# Revit family: Casement_36_G_Top_Hung_Standard
name_source: partatom
category: Windows
revit_build: Autodesk Revit 2014 (Build: 20130308_1515(x64)
units: mm (PartAtom-declared; Revit-internal decimal feet)

## types (12) — shared parameters
Aluminium Thickness = 1 mm  [stored 0.00328084 ft]
Bead SG Gap = 13 mm  [stored 0.0426509 ft]
Bottom Hung = No
Casement Dimension = 36 mm  [stored 0.11811 ft]
Custom Sash Height Bottom = 569 mm  [stored 1.8668 ft]
Custom Sash Height Top = 569 mm  [stored 1.8668 ft]
Custom Window Height = 1190 mm  [stored 3.9042 ft]
DG Extrusion Start = 8 mm  [stored 0.0262467 ft]
DG Gasket Finish = Double Glazing Gasket Material
DG Thickness Calc = 4 mm  [stored 0.0131234 ft]
Default Sill Height = 800 mm  [stored 2.62467 ft]
Depth Bead = 22 mm  [stored 0.0721785 ft]
Description = Window 36mm, Type G top hung
Frame Center Offset = 18 mm  [stored 0.0590551 ft]
Height = 1200 mm  [stored 3.93701 ft]
Height Panel 1 = 555 mm  [stored 1.82087 ft]
Height Panel 2 = 555 mm  [stored 1.82087 ft]
Height Panel 4 = 1140 mm  [stored 3.74016 ft]
Height Sash 1 = 539 mm
Height Sash 2 = 539 mm
Height Sash Bottom Opening = 569 mm  [stored 1.8668 ft]
Height Sash Top Opening = 569 mm  [stored 1.8668 ft]
Length Mullion = 1200 mm  [stored 3.93701 ft]
Limit Fixed Pane Height Max = 1800 mm
Limit Fixed Pane Height Min = 200 mm  [stored 0.656168 ft]
Limit Fixed Pane Width Max = 1500 mm
Limit Fixed Pane Width Min = 200 mm  [stored 0.656168 ft]
Limit Sash Bottom Height Max Based On Top Sash = 1229 mm
Limit Sash Height Bottom Max = 900 mm  [stored 2.95276 ft]
Limit Sash Height Bottom Min = 300 mm  [stored 0.984252 ft]
Limit Sash Height Top Max = 900 mm  [stored 2.95276 ft]
Limit Sash Height Top Min = 300 mm  [stored 0.984252 ft]
Limit Sash Width Max = 1200 mm  [stored 3.93701 ft]
Limit Sash Width Min = 300 mm  [stored 0.984252 ft]
Limit Window Height Max = 1860 mm
Manufacturer = Crealco
Max System DG One Piece Thickness = 6 mm  [stored 0.019685 ft]
Max System DG Unit Thickness = 25 mm  [stored 0.082021 ft]
Model = Casement 36
Offset Bead SG Center Reversed = 18 mm  [stored 0.0590551 ft]
Offset Sash 1 Top = 23 mm  [stored 0.0754593 ft]
Offset Sash 2 Top = 608 mm  [stored 1.99475 ft]
Offset Sash Left = 23 mm  [stored 0.0754593 ft]
Offset Transom 1 Top = 585 mm  [stored 1.91929 ft]
Offset Window Exterior = 18 mm  [stored 0.0590551 ft]
Rough Width = 16 mm  [stored 0.0524934 ft]
SG Gasket Thickness = 6 mm  [stored 0.019685 ft]
Sash Center Offset = 15 mm  [stored 0.0492126 ft]
Sash Overlap = 7 mm  [stored 0.0229659 ft]
Sash Spacing Inner = 8 mm  [stored 0.0262467 ft]
Top Hung = Yes
URL = http://www.crealco.co.za
Wall Closure = By host
Width Bead = 15 mm  [stored 0.0492126 ft]
Width Profile = 30 mm  [stored 0.0984252 ft]
zero-valued in all types: Window Exterior Offset

## per-type parameters (varying)
- 36-1212DT-1000Pa: Area Pane Left Bottom=0.25 m²; Area Pane Left Top=0.25 m²; Area Pane Right=0.6 m²; Clearvue Insulated LowE SHGC Value=0.639; Clearvue Insulated LowE U Value=4.92; Clearvue Insulated SHGC Value=0.7; Clearvue Insulated U Value=5.59; Clearvue SHGC Value=0.796; Clearvue U Value=8.34; Custom Sash Width=569 mm  [stored 1.8668 ft]; Custom Windload=1000 mm  [stored 3.28084 ft]; Custom Window Width=1190 mm  [stored 3.9042 ft]; Depth Mullion=37 mm  [stored 0.121391 ft]; Energy Advantage SHGC Value=0.714; Energy Advantage U Value=6.46; Intruderprufe Insulated LowE SHGC Value=0.591; Intruderprufe Insulated LowE U Value=4.81; Intruderprufe Insulated SHGC Value=0.643; Intruderprufe Insulated U Value=5.45; Intruderprufe LowE SHGC Value=0.669; Intruderprufe LowE U Value=6.31; Intruderprufe SHGC Value=0.759; Intruderprufe U Value=8.16; Length Transom=555 mm  [stored 1.82087 ft]; Limit Window Width Max=2145 mm; Limit Window Width Min=845 mm  [stored 2.77231 ft]; Max Pane Area=0.6 m²; Mullion Depth Windload Based=37 mm  [stored 0.121391 ft]; Offset Mullion Left=585 mm  [stored 1.91929 ft]; Offset Panel 4 Left=615 mm  [stored 2.01772 ft]; Width=1190 mm  [stored 3.9042 ft]; Width Panel 1=555 mm  [stored 1.82087 ft]; Width Panel 2=555 mm  [stored 1.82087 ft]; Width Panel 4=545 mm; Width Sash 1=539 mm; Width Sash 2=539 mm; Width Sash Opening=569 mm  [stored 1.8668 ft]; Windload Design=1000 mm  [stored 3.28084 ft]
- 36-1512DT-1000Pa: Area Pane Left Bottom=0.25 m²; Area Pane Left Top=0.25 m²; Area Pane Right=0.94 m²; Clearvue Insulated LowE SHGC Value=0.73; Clearvue Insulated LowE U Value=4.85; Clearvue Insulated SHGC Value=0.8; Clearvue Insulated U Value=5.63; Clearvue SHGC Value=0.909; Clearvue U Value=8.83; Custom Sash Width=569 mm  [stored 1.8668 ft]; Custom Windload=1000 mm  [stored 3.28084 ft]; Custom Window Width=1490 mm; Depth Mullion=37 mm  [stored 0.121391 ft]; Energy Advantage SHGC Value=0.814; Energy Advantage U Value=6.64; Intruderprufe Insulated LowE SHGC Value=0.671; Intruderprufe Insulated LowE U Value=4.74; Intruderprufe Insulated SHGC Value=0.734; Intruderprufe Insulated U Value=5.49; Intruderprufe LowE SHGC Value=0.763; Intruderprufe LowE U Value=6.48; Intruderprufe SHGC Value=0.865; Intruderprufe U Value=8.64; Length Transom=555 mm  [stored 1.82087 ft]; Limit Window Width Max=2145 mm; Limit Window Width Min=845 mm  [stored 2.77231 ft]; Max Pane Area=0.94 m²; Mullion Depth Windload Based=37 mm  [stored 0.121391 ft]; Offset Mullion Left=585 mm  [stored 1.91929 ft]; Offset Panel 4 Left=615 mm  [stored 2.01772 ft]; Width=1490 mm; Width Panel 1=555 mm  [stored 1.82087 ft]; Width Panel 2=555 mm  [stored 1.82087 ft]; Width Panel 4=845 mm  [stored 2.77231 ft]; Width Sash 1=539 mm; Width Sash 2=539 mm; Width Sash Opening=569 mm  [stored 1.8668 ft]; Windload Design=1000 mm  [stored 3.28084 ft]
- 36-1812DT-1000Pa: Area Pane Left Bottom=0.41 m²; Area Pane Left Top=0.41 m²; Area Pane Right=0.91 m²; Clearvue Insulated LowE SHGC Value=0.687; Clearvue Insulated LowE U Value=4.47; Clearvue Insulated SHGC Value=0.753; Clearvue Insulated U Value=5.2; Clearvue SHGC Value=0.855; Clearvue U Value=8.22; Custom Sash Width=900 mm  [stored 2.95276 ft]; Custom Windload=1000 mm  [stored 3.28084 ft]; Custom Window Width=1790 mm; Depth Mullion=37 mm  [stored 0.121391 ft]; Energy Advantage SHGC Value=0.766; Energy Advantage U Value=6.15; Intruderprufe Insulated LowE SHGC Value=0.631; Intruderprufe Insulated LowE U Value=4.37; Intruderprufe Insulated SHGC Value=0.691; Intruderprufe Insulated U Value=5.08; Intruderprufe LowE SHGC Value=0.717; Intruderprufe LowE U Value=6.01; Intruderprufe SHGC Value=0.814; Intruderprufe U Value=8.04; Length Transom=886 mm  [stored 2.90682 ft]; Limit Window Width Max=2476 mm; Limit Window Width Min=1176 mm  [stored 3.85827 ft]; Max Pane Area=0.91 m²; Mullion Depth Windload Based=37 mm  [stored 0.121391 ft]; Offset Mullion Left=916 mm  [stored 3.00525 ft]; Offset Panel 4 Left=946 mm; Width=1790 mm; Width Panel 1=886 mm  [stored 2.90682 ft]; Width Panel 2=886 mm  [stored 2.90682 ft]; Width Panel 4=814 mm; Width Sash 1=870 mm  [stored 2.85433 ft]; Width Sash 2=870 mm  [stored 2.85433 ft]; Width Sash Opening=900 mm  [stored 2.95276 ft]; Windload Design=1000 mm  [stored 3.28084 ft]
- 36-2412DT-1000Pa: Area Pane Left Bottom=0.41 m²; Area Pane Left Top=0.41 m²; Area Pane Right=1.59 m²; Clearvue Insulated LowE SHGC Value=0.543; Clearvue Insulated LowE U Value=3.08; Clearvue Insulated SHGC Value=0.597; Clearvue Insulated U Value=3.67; Clearvue SHGC Value=0; Clearvue U Value=7.9; Custom Sash Width=900 mm  [stored 2.95276 ft]; Custom Windload=1000 mm  [stored 3.28084 ft]; Custom Window Width=2390 mm; Depth Mullion=37 mm  [stored 0.121391 ft]; Energy Advantage SHGC Value=0; Energy Advantage U Value=7.9; Intruderprufe Insulated LowE SHGC Value=0.499; Intruderprufe Insulated LowE U Value=3.01; Intruderprufe Insulated SHGC Value=0.548; Intruderprufe Insulated U Value=3.58; Intruderprufe LowE SHGC Value=0.567; Intruderprufe LowE U Value=4.33; Intruderprufe SHGC Value=0.644; Intruderprufe U Value=5.95; Length Transom=886 mm  [stored 2.90682 ft]; Limit Window Width Max=2476 mm; Limit Window Width Min=1176 mm  [stored 3.85827 ft]; Max Pane Area=1.59 m²; Mullion Depth Windload Based=37 mm  [stored 0.121391 ft]; Offset Mullion Left=916 mm  [stored 3.00525 ft]; Offset Panel 4 Left=946 mm; Width=2390 mm; Width Panel 1=886 mm  [stored 2.90682 ft]; Width Panel 2=886 mm  [stored 2.90682 ft]; Width Panel 4=1414 mm; Width Sash 1=870 mm  [stored 2.85433 ft]; Width Sash 2=870 mm  [stored 2.85433 ft]; Width Sash Opening=900 mm  [stored 2.95276 ft]; Windload Design=1000 mm  [stored 3.28084 ft]
- 36-1212DT-1500Pa: Area Pane Left Bottom=0.25 m²; Area Pane Left Top=0.25 m²; Area Pane Right=0.6 m²; Clearvue Insulated LowE SHGC Value=0.639; Clearvue Insulated LowE U Value=4.92; Clearvue Insulated SHGC Value=0.7; Clearvue Insulated U Value=5.59; Clearvue SHGC Value=0.796; Clearvue U Value=8.34; Custom Sash Width=569 mm  [stored 1.8668 ft]; Custom Windload=1500 mm; Custom Window Width=1190 mm  [stored 3.9042 ft]; Depth Mullion=37 mm  [stored 0.121391 ft]; Energy Advantage SHGC Value=0.714; Energy Advantage U Value=6.46; Intruderprufe Insulated LowE SHGC Value=0.591; Intruderprufe Insulated LowE U Value=4.81; Intruderprufe Insulated SHGC Value=0.643; Intruderprufe Insulated U Value=5.45; Intruderprufe LowE SHGC Value=0.669; Intruderprufe LowE U Value=6.31; Intruderprufe SHGC Value=0.759; Intruderprufe U Value=8.16; Length Transom=555 mm  [stored 1.82087 ft]; Limit Window Width Max=2145 mm; Limit Window Width Min=845 mm  [stored 2.77231 ft]; Max Pane Area=0.6 m²; Mullion Depth Windload Based=37 mm  [stored 0.121391 ft]; Offset Mullion Left=585 mm  [stored 1.91929 ft]; Offset Panel 4 Left=615 mm  [stored 2.01772 ft]; Width=1190 mm  [stored 3.9042 ft]; Width Panel 1=555 mm  [stored 1.82087 ft]; Width Panel 2=555 mm  [stored 1.82087 ft]; Width Panel 4=545 mm; Width Sash 1=539 mm; Width Sash 2=539 mm; Width Sash Opening=569 mm  [stored 1.8668 ft]; Windload Design=1500 mm
- 36-1212DT-2000Pa: Area Pane Left Bottom=0.25 m²; Area Pane Left Top=0.25 m²; Area Pane Right=0.6 m²; Clearvue Insulated LowE SHGC Value=0.639; Clearvue Insulated LowE U Value=4.96; Clearvue Insulated SHGC Value=0.701; Clearvue Insulated U Value=5.62; Clearvue SHGC Value=0.798; Clearvue U Value=8.4; Custom Sash Width=569 mm  [stored 1.8668 ft]; Custom Windload=2000 mm; Custom Window Width=1190 mm  [stored 3.9042 ft]; Depth Mullion=54 mm  [stored 0.177165 ft]; Energy Advantage SHGC Value=0.716; Energy Advantage U Value=6.53; Intruderprufe Insulated LowE SHGC Value=0.59; Intruderprufe Insulated LowE U Value=4.86; Intruderprufe Insulated SHGC Value=0.644; Intruderprufe Insulated U Value=5.5; Intruderprufe LowE SHGC Value=0.671; Intruderprufe LowE U Value=6.39; Intruderprufe SHGC Value=0.762; Intruderprufe U Value=8.23; Length Transom=555 mm  [stored 1.82087 ft]; Limit Window Width Max=2145 mm; Limit Window Width Min=845 mm  [stored 2.77231 ft]; Max Pane Area=0.6 m²; Mullion Depth Windload Based=54 mm  [stored 0.177165 ft]; Offset Mullion Left=585 mm  [stored 1.91929 ft]; Offset Panel 4 Left=615 mm  [stored 2.01772 ft]; Width=1190 mm  [stored 3.9042 ft]; Width Panel 1=555 mm  [stored 1.82087 ft]; Width Panel 2=555 mm  [stored 1.82087 ft]; Width Panel 4=545 mm; Width Sash 1=539 mm; Width Sash 2=539 mm; Width Sash Opening=569 mm  [stored 1.8668 ft]; Windload Design=2000 mm
- 36-1512DT-1500Pa: Area Pane Left Bottom=0.25 m²; Area Pane Left Top=0.25 m²; Area Pane Right=0.94 m²; Clearvue Insulated LowE SHGC Value=0.728; Clearvue Insulated LowE U Value=4.91; Clearvue Insulated SHGC Value=0.799; Clearvue Insulated U Value=5.68; Clearvue SHGC Value=0.908; Clearvue U Value=8.87; Custom Sash Width=569 mm  [stored 1.8668 ft]; Custom Windload=1500 mm; Custom Window Width=1490 mm; Depth Mullion=54 mm  [stored 0.177165 ft]; Energy Advantage SHGC Value=0.813; Energy Advantage U Value=6.68; Intruderprufe Insulated LowE SHGC Value=0.672; Intruderprufe Insulated LowE U Value=4.8; Intruderprufe Insulated SHGC Value=0.733; Intruderprufe Insulated U Value=5.55; Intruderprufe LowE SHGC Value=0.761; Intruderprufe LowE U Value=6.53; Intruderprufe SHGC Value=0.864; Intruderprufe U Value=8.67; Length Transom=555 mm  [stored 1.82087 ft]; Limit Window Width Max=2145 mm; Limit Window Width Min=845 mm  [stored 2.77231 ft]; Max Pane Area=0.94 m²; Mullion Depth Windload Based=54 mm  [stored 0.177165 ft]; Offset Mullion Left=585 mm  [stored 1.91929 ft]; Offset Panel 4 Left=615 mm  [stored 2.01772 ft]; Width=1490 mm; Width Panel 1=555 mm  [stored 1.82087 ft]; Width Panel 2=555 mm  [stored 1.82087 ft]; Width Panel 4=845 mm  [stored 2.77231 ft]; Width Sash 1=539 mm; Width Sash 2=539 mm; Width Sash Opening=569 mm  [stored 1.8668 ft]; Windload Design=1500 mm
- 36-1512DT-2000Pa: Area Pane Left Bottom=0.25 m²; Area Pane Left Top=0.25 m²; Area Pane Right=0.94 m²; Clearvue Insulated LowE SHGC Value=0.728; Clearvue Insulated LowE U Value=4.91; Clearvue Insulated SHGC Value=0.799; Clearvue Insulated U Value=5.68; Clearvue SHGC Value=0.908; Clearvue U Value=8.87; Custom Sash Width=569 mm  [stored 1.8668 ft]; Custom Windload=2000 mm; Custom Window Width=1490 mm; Depth Mullion=54 mm  [stored 0.177165 ft]; Energy Advantage SHGC Value=0.813; Energy Advantage U Value=6.68; Intruderprufe Insulated LowE SHGC Value=0.672; Intruderprufe Insulated LowE U Value=4.8; Intruderprufe Insulated SHGC Value=0.733; Intruderprufe Insulated U Value=5.55; Intruderprufe LowE SHGC Value=0.761; Intruderprufe LowE U Value=6.53; Intruderprufe SHGC Value=0.864; Intruderprufe U Value=8.67; Length Transom=555 mm  [stored 1.82087 ft]; Limit Window Width Max=2145 mm; Limit Window Width Min=845 mm  [stored 2.77231 ft]; Max Pane Area=0.94 m²; Mullion Depth Windload Based=54 mm  [stored 0.177165 ft]; Offset Mullion Left=585 mm  [stored 1.91929 ft]; Offset Panel 4 Left=615 mm  [stored 2.01772 ft]; Width=1490 mm; Width Panel 1=555 mm  [stored 1.82087 ft]; Width Panel 2=555 mm  [stored 1.82087 ft]; Width Panel 4=845 mm  [stored 2.77231 ft]; Width Sash 1=539 mm; Width Sash 2=539 mm; Width Sash Opening=569 mm  [stored 1.8668 ft]; Windload Design=2000 mm
- 36-1812DT-1500Pa: Area Pane Left Bottom=0.41 m²; Area Pane Left Top=0.41 m²; Area Pane Right=0.91 m²; Clearvue Insulated LowE SHGC Value=0.685; Clearvue Insulated LowE U Value=4.51; Clearvue Insulated SHGC Value=0.752; Clearvue Insulated U Value=5.25; Clearvue SHGC Value=0.854; Clearvue U Value=8.25; Custom Sash Width=900 mm  [stored 2.95276 ft]; Custom Windload=1500 mm; Custom Window Width=1790 mm; Depth Mullion=54 mm  [stored 0.177165 ft]; Energy Advantage SHGC Value=0.765; Energy Advantage U Value=6.19; Intruderprufe Insulated LowE SHGC Value=0.632; Intruderprufe Insulated LowE U Value=4.41; Intruderprufe Insulated SHGC Value=0.69; Intruderprufe Insulated U Value=5.12; Intruderprufe LowE SHGC Value=0.716; Intruderprufe LowE U Value=6.05; Intruderprufe SHGC Value=0.813; Intruderprufe U Value=8.07; Length Transom=886 mm  [stored 2.90682 ft]; Limit Window Width Max=2476 mm; Limit Window Width Min=1176 mm  [stored 3.85827 ft]; Max Pane Area=0.91 m²; Mullion Depth Windload Based=54 mm  [stored 0.177165 ft]; Offset Mullion Left=916 mm  [stored 3.00525 ft]; Offset Panel 4 Left=946 mm; Width=1790 mm; Width Panel 1=886 mm  [stored 2.90682 ft]; Width Panel 2=886 mm  [stored 2.90682 ft]; Width Panel 4=814 mm; Width Sash 1=870 mm  [stored 2.85433 ft]; Width Sash 2=870 mm  [stored 2.85433 ft]; Width Sash Opening=900 mm  [stored 2.95276 ft]; Windload Design=1500 mm
- 36-1812DT-2000Pa: Area Pane Left Bottom=0.41 m²; Area Pane Left Top=0.41 m²; Area Pane Right=0.91 m²; Clearvue Insulated LowE SHGC Value=0.685; Clearvue Insulated LowE U Value=4.51; Clearvue Insulated SHGC Value=0.752; Clearvue Insulated U Value=5.25; Clearvue SHGC Value=0.854; Clearvue U Value=8.25; Custom Sash Width=900 mm  [stored 2.95276 ft]; Custom Windload=2000 mm; Custom Window Width=1790 mm; Depth Mullion=54 mm  [stored 0.177165 ft]; Energy Advantage SHGC Value=0.765; Energy Advantage U Value=6.19; Intruderprufe Insulated LowE SHGC Value=0.632; Intruderprufe Insulated LowE U Value=4.41; Intruderprufe Insulated SHGC Value=0.69; Intruderprufe Insulated U Value=5.12; Intruderprufe LowE SHGC Value=0.716; Intruderprufe LowE U Value=6.05; Intruderprufe SHGC Value=0.813; Intruderprufe U Value=8.07; Length Transom=886 mm  [stored 2.90682 ft]; Limit Window Width Max=2476 mm; Limit Window Width Min=1176 mm  [stored 3.85827 ft]; Max Pane Area=0.91 m²; Mullion Depth Windload Based=54 mm  [stored 0.177165 ft]; Offset Mullion Left=916 mm  [stored 3.00525 ft]; Offset Panel 4 Left=946 mm; Width=1790 mm; Width Panel 1=886 mm  [stored 2.90682 ft]; Width Panel 2=886 mm  [stored 2.90682 ft]; Width Panel 4=814 mm; Width Sash 1=870 mm  [stored 2.85433 ft]; Width Sash 2=870 mm  [stored 2.85433 ft]; Width Sash Opening=900 mm  [stored 2.95276 ft]; Windload Design=2000 mm
- 36-2412DT-1500Pa: Area Pane Left Bottom=0.41 m²; Area Pane Left Top=0.41 m²; Area Pane Right=1.59 m²; Clearvue Insulated LowE SHGC Value=0.542; Clearvue Insulated LowE U Value=3.11; Clearvue Insulated SHGC Value=0.596; Clearvue Insulated U Value=3.7; Clearvue SHGC Value=0; Clearvue U Value=7.9; Custom Sash Width=900 mm  [stored 2.95276 ft]; Custom Windload=1500 mm; Custom Window Width=2390 mm; Depth Mullion=54 mm  [stored 0.177165 ft]; Energy Advantage SHGC Value=0; Energy Advantage U Value=7.9; Intruderprufe Insulated LowE SHGC Value=0.499; Intruderprufe Insulated LowE U Value=3.04; Intruderprufe Insulated SHGC Value=0.547; Intruderprufe Insulated U Value=3.62; Intruderprufe LowE SHGC Value=0.566; Intruderprufe LowE U Value=4.36; Intruderprufe SHGC Value=0.644; Intruderprufe U Value=5.95; Length Transom=886 mm  [stored 2.90682 ft]; Limit Window Width Max=2476 mm; Limit Window Width Min=1176 mm  [stored 3.85827 ft]; Max Pane Area=1.59 m²; Mullion Depth Windload Based=54 mm  [stored 0.177165 ft]; Offset Mullion Left=916 mm  [stored 3.00525 ft]; Offset Panel 4 Left=946 mm; Width=2390 mm; Width Panel 1=886 mm  [stored 2.90682 ft]; Width Panel 2=886 mm  [stored 2.90682 ft]; Width Panel 4=1414 mm; Width Sash 1=870 mm  [stored 2.85433 ft]; Width Sash 2=870 mm  [stored 2.85433 ft]; Width Sash Opening=900 mm  [stored 2.95276 ft]; Windload Design=1500 mm
- 36-2412DT-2000Pa: Area Pane Left Bottom=0.41 m²; Area Pane Left Top=0.41 m²; Area Pane Right=1.59 m²; Clearvue Insulated LowE SHGC Value=0.542; Clearvue Insulated LowE U Value=3.11; Clearvue Insulated SHGC Value=0.596; Clearvue Insulated U Value=3.7; Clearvue SHGC Value=0; Clearvue U Value=7.9; Custom Sash Width=900 mm  [stored 2.95276 ft]; Custom Windload=2000 mm; Custom Window Width=2390 mm; Depth Mullion=54 mm  [stored 0.177165 ft]; Energy Advantage SHGC Value=0; Energy Advantage U Value=7.9; Intruderprufe Insulated LowE SHGC Value=0.499; Intruderprufe Insulated LowE U Value=3.04; Intruderprufe Insulated SHGC Value=0.547; Intruderprufe Insulated U Value=3.62; Intruderprufe LowE SHGC Value=0.566; Intruderprufe LowE U Value=4.36; Intruderprufe SHGC Value=0.644; Intruderprufe U Value=5.95; Length Transom=886 mm  [stored 2.90682 ft]; Limit Window Width Max=2476 mm; Limit Window Width Min=1176 mm  [stored 3.85827 ft]; Max Pane Area=1.59 m²; Mullion Depth Windload Based=54 mm  [stored 0.177165 ft]; Offset Mullion Left=916 mm  [stored 3.00525 ft]; Offset Panel 4 Left=946 mm; Width=2390 mm; Width Panel 1=886 mm  [stored 2.90682 ft]; Width Panel 2=886 mm  [stored 2.90682 ft]; Width Panel 4=1414 mm; Width Sash 1=870 mm  [stored 2.85433 ft]; Width Sash 2=870 mm  [stored 2.85433 ft]; Width Sash Opening=900 mm  [stored 2.95276 ft]; Windload Design=2000 mm

note: [stored X ft] marks values corroborated as IEEE doubles in the binary element streams (Revit-internal decimal feet)

## geometry (parser evidence)
native form markers: Blend x4, Extrusion x1, Sweep x28
no freeform markers — native parametric forms only
